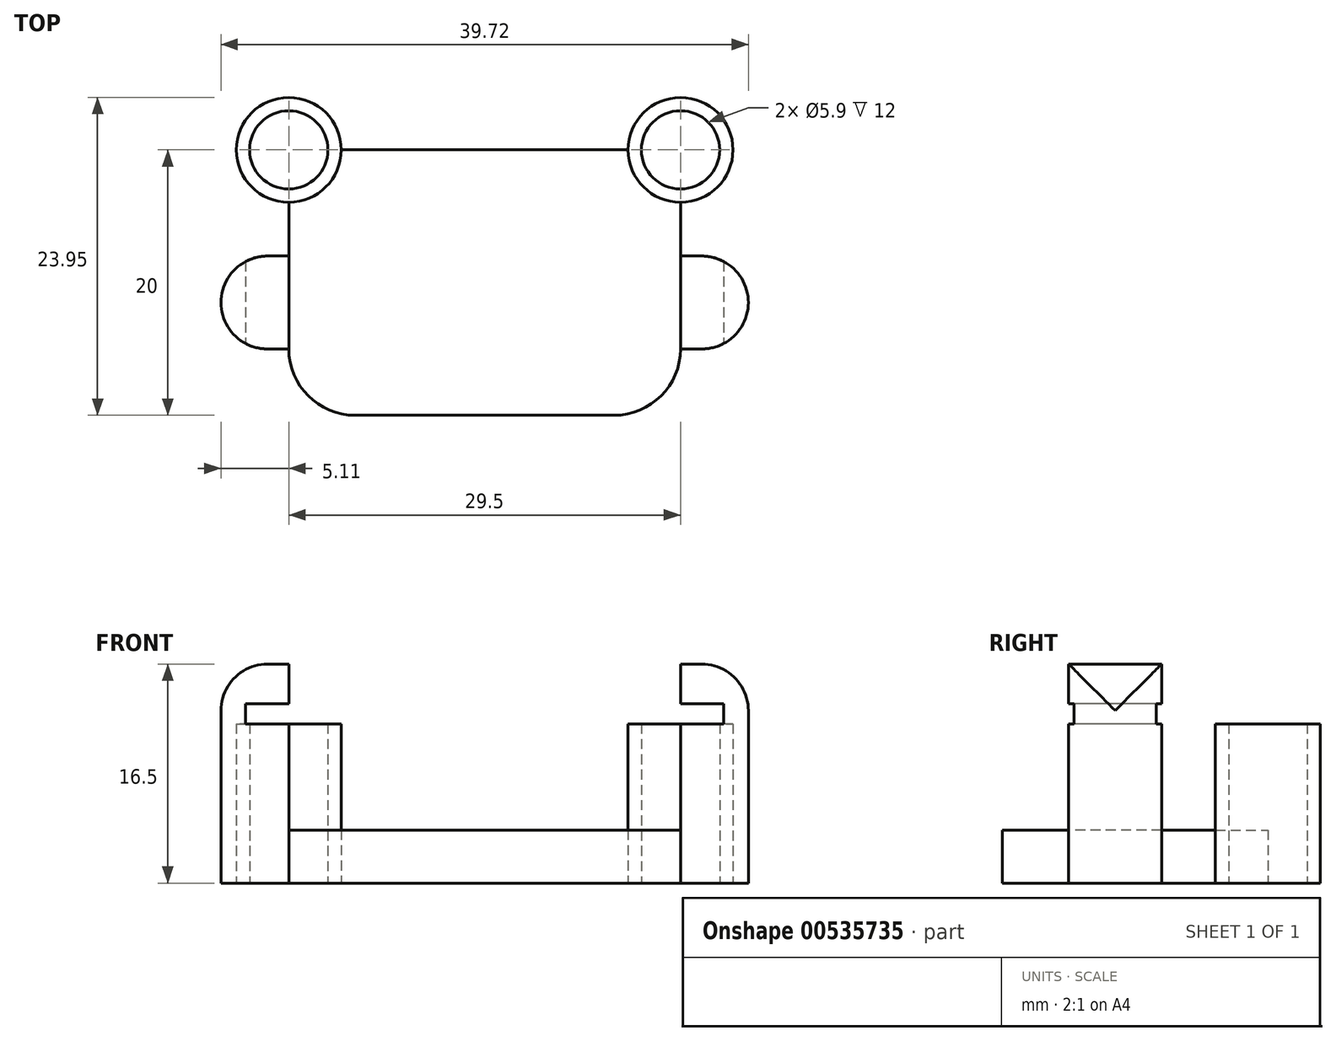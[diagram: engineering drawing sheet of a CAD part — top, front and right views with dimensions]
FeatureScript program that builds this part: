
annotation { "Feature Type Name" : "Feature", "Feature Type Description" : "" }
export const myFeature = defineFeature(function(context is Context, id is Id, definition is map)
    precondition{}
    {
        {
            var Q0;
            Q0=qCreatedBy(makeId("Top.planeOp"),FACE);
            var sketch = newSketch(context, id + "F0", { "sketchPlane" : qUnion([Q0])});
            skCircle(sketch, "E0", {"center": v(0, 0) * mm, "radius": 2.95 * mm});
            skCircle(sketch, "E1", {"center": v(29.5, 0) * mm, "radius": 2.95 * mm});
            skCircle(sketch, "E2", {"center": v(0, 0) * mm, "radius": 3.95 * mm});
            skCircle(sketch, "E3", {"center": v(29.5, 0) * mm, "radius": 3.95 * mm});
            skSolve(sketch);
        }
        {
            var Q0;
            Q0=makeQuery(id+"F0.imprint","IMPRINT",FACE,{"disambiguationData":[TD([[makeQuery(id+"F0.imprint","IMPRINT",EDGE,{"derivedFrom":sQuery(id+"F0.wireOp",EDGE,"E0")}),-1.0]])]});
            var Q1;
            Q1=makeQuery(id+"F0.imprint","IMPRINT",FACE,{"disambiguationData":[TD([[makeQuery(id+"F0.imprint","IMPRINT",EDGE,{"derivedFrom":sQuery(id+"F0.wireOp",EDGE,"E1")}),-1.0]])]});
            extrude(context, id + "F1", {"entities" : qUnion([Q0, Q1]), "depth" : 12 * mm, "offsetDistance" : 25 * mm});
        }
        {
            var Q0;
            Q0=makeQuery(id+"F1.opExtrude","CAP_FACE",FACE,{"disambiguationData":[OSD([sQuery(id+"F0.wireOp",EDGE,"E0"),sQuery(id+"F0.wireOp",EDGE,"E2")])],"isStart":true});
            var sketch = newSketch(context, id + "F2", { "sketchPlane" : qUnion([Q0])});
            skCircle(sketch, "E4.0.0", {"center": v(0, 0) * mm, "radius": 3.95 * mm});
            skCircle(sketch, "E5.0.0", {"center": v(29.5, 0) * mm, "radius": 3.95 * mm});
            skLineSegment(sketch, "E6.bottom", {"start": v(0, 0) * mm, "end": v(29.5, 0) * mm});
            skLineSegment(sketch, "E6.top", {"start": v(0, 20) * mm, "end": v(29.5, 20) * mm});
            skLineSegment(sketch, "E6.left", {"start": v(0, 0) * mm, "end": v(0, 20) * mm});
            skLineSegment(sketch, "E6.right", {"start": v(29.5, 0) * mm, "end": v(29.5, 20) * mm});
            skSolve(sketch);
        }
        {
            var Q0;
            {var subQ0=sQuery(id+"F2.wireOp",EDGE,"E6.top");Q0=makeQuery(id+"F2.imprint","IMPRINT",FACE,{"disambiguationData":[TD([[makeQuery(id+"F2.imprint","IMPRINT",EDGE,{"derivedFrom":subQ0}),-1.0]])]});}
            extrude(context, id + "F3", {"entities" : qUnion([Q0]), "oppositeDirection" : true, "depth" : 4 * mm, "offsetDistance" : 25 * mm});
        }
        {
            var Q0;
            Q0=makeQuery(id+"F3.opExtrude","SWEPT_BODY",BODY,{"disambiguationData":[OSD([sQuery(id+"F2.wireOp",EDGE,"E4.0.0"),sQuery(id+"F2.wireOp",EDGE,"E5.0.0"),sQuery(id+"F2.wireOp",EDGE,"E6.bottom"),sQuery(id+"F2.wireOp",EDGE,"E6.top"),sQuery(id+"F2.wireOp",EDGE,"E6.left"),sQuery(id+"F2.wireOp",EDGE,"E6.right")])]});
            var Q1;
            Q1=makeQuery(id+"F1.opExtrude","SWEPT_BODY",BODY,{"disambiguationData":[OSD([sQuery(id+"F0.wireOp",EDGE,"E0"),sQuery(id+"F0.wireOp",EDGE,"E2")])]});
            var Q2;
            Q2=makeQuery(id+"F1.opExtrude","SWEPT_BODY",BODY,{"disambiguationData":[OSD([sQuery(id+"F0.wireOp",EDGE,"E1"),sQuery(id+"F0.wireOp",EDGE,"E3")])]});
            booleanBodies(context, id + "F4", {"operationType" : BooleanOperationType.UNION, "tools" : qUnion([Q0, Q1, Q2])});
        }
        {
            var Q0;
            Q0=makeQuery(id+"F3.opExtrude","SWEPT_EDGE",EDGE,{"disambiguationData":[OSD([sQuery(id+"F2.wireOp",EDGE,"E6.top"),sQuery(id+"F2.wireOp",EDGE,"E6.left")])]});
            var Q1;
            Q1=makeQuery(id+"F3.opExtrude","SWEPT_EDGE",EDGE,{"disambiguationData":[OSD([sQuery(id+"F2.wireOp",EDGE,"E6.top"),sQuery(id+"F2.wireOp",EDGE,"E6.right")])]});
            fillet(context, id + "F5", {"entities" : qUnion([Q0, Q1]), "radius" : 5 * mm, "tangentPropagation" : true, "allowEdgeOverflow" : false});
        }
        {
            var Q0;
            Q0=makeQuery(id+"F4.opBoolean","MERGE",FACE,{"derivedFrom":[makeQuery(id+"F1.opExtrude","CAP_FACE",FACE,{"disambiguationData":[OSD([sQuery(id+"F0.wireOp",EDGE,"E0"),sQuery(id+"F0.wireOp",EDGE,"E2")])],"isStart":true}),makeQuery(id+"F1.opExtrude","CAP_FACE",FACE,{"disambiguationData":[OSD([sQuery(id+"F0.wireOp",EDGE,"E1"),sQuery(id+"F0.wireOp",EDGE,"E3")])],"isStart":true}),makeQuery(id+"F3.opExtrude","CAP_FACE",FACE,{"disambiguationData":[OSD([sQuery(id+"F2.wireOp",EDGE,"E4.0.0"),sQuery(id+"F2.wireOp",EDGE,"E5.0.0"),sQuery(id+"F2.wireOp",EDGE,"E6.bottom"),sQuery(id+"F2.wireOp",EDGE,"E6.top"),sQuery(id+"F2.wireOp",EDGE,"E6.left"),sQuery(id+"F2.wireOp",EDGE,"E6.right")])],"isStart":true})]});
            var sketch = newSketch(context, id + "F6", { "sketchPlane" : qUnion([Q0])});
            skLineSegment(sketch, "E7.0.0", {"start": v(29.5, 3.95) * mm, "end": v(29.5, 15) * mm});
            skArc(sketch, "E7.0.1", {"start": v(29.5, 15) * mm, "mid": v(28.04, 18.54) * mm, "end": v(24.5, 20) * mm});
            skLineSegment(sketch, "E7.0.2", {"start": v(24.5, 20) * mm, "end": v(5, 20) * mm});
            skArc(sketch, "E7.0.3", {"start": v(5, 20) * mm, "mid": v(1.46, 18.54) * mm, "end": v(0, 15) * mm});
            skLineSegment(sketch, "E7.0.4", {"start": v(0, 15) * mm, "end": v(0, 3.95) * mm});
            skArc(sketch, "E7.0.5", {"start": v(0, 3.95) * mm, "mid": v(-2.8, -2.8) * mm, "end": v(3.95, 0) * mm});
            skLineSegment(sketch, "E7.0.6", {"start": v(3.95, 0) * mm, "end": v(25.55, 0) * mm});
            skArc(sketch, "E7.0.7", {"start": v(25.55, 0) * mm, "mid": v(32.3, -2.8) * mm, "end": v(29.5, 3.95) * mm});
            skLineSegment(sketch, "E8.bottom", {"start": v(0, 15) * mm, "end": v(-2.11, 15) * mm});
            skLineSegment(sketch, "E8.top", {"start": v(0, 8) * mm, "end": v(-2.11, 8) * mm});
            skLineSegment(sketch, "E8.left", {"start": v(0, 15) * mm, "end": v(0, 8) * mm});
            skLineSegment(sketch, "E8.right", {"start": v(-2.11, 15) * mm, "end": v(-2.11, 8) * mm});
            skLineSegment(sketch, "E9.bottom", {"start": v(29.5, 15) * mm, "end": v(31.61, 15) * mm});
            skLineSegment(sketch, "E9.top", {"start": v(29.5, 8) * mm, "end": v(31.61, 8) * mm});
            skLineSegment(sketch, "E9.left", {"start": v(29.5, 15) * mm, "end": v(29.5, 8) * mm});
            skLineSegment(sketch, "E9.right", {"start": v(31.61, 15) * mm, "end": v(31.61, 8) * mm});
            skLineSegment(sketch, "E10.bottom", {"start": v(-2.11, 8) * mm, "end": v(-5.11, 8) * mm});
            skLineSegment(sketch, "E10.top", {"start": v(-2.11, 15) * mm, "end": v(-5.11, 15) * mm});
            skLineSegment(sketch, "E10.left", {"start": v(-2.11, 8) * mm, "end": v(-2.11, 15) * mm});
            skLineSegment(sketch, "E10.right", {"start": v(-5.11, 8) * mm, "end": v(-5.11, 15) * mm});
            skLineSegment(sketch, "E11.bottom", {"start": v(31.61, 8) * mm, "end": v(34.61, 8) * mm});
            skLineSegment(sketch, "E11.top", {"start": v(31.61, 15) * mm, "end": v(34.61, 15) * mm});
            skLineSegment(sketch, "E11.left", {"start": v(31.61, 8) * mm, "end": v(31.61, 15) * mm});
            skLineSegment(sketch, "E11.right", {"start": v(34.61, 8) * mm, "end": v(34.61, 15) * mm});
            skSolve(sketch);
        }
        {
            var Q0;
            Q0=makeQuery(id+"F6.imprint","IMPRINT",FACE,{"disambiguationData":[TD([[makeQuery(id+"F6.imprint","IMPRINT",EDGE,{"derivedFrom":sQuery(id+"F6.wireOp",EDGE,"E10.bottom")}),-1.0]])]});
            var Q1;
            Q1=makeQuery(id+"F6.imprint","IMPRINT",FACE,{"disambiguationData":[TD([[makeQuery(id+"F6.imprint","IMPRINT",EDGE,{"derivedFrom":sQuery(id+"F6.wireOp",EDGE,"E8.bottom")}),1.0]])]});
            var Q2;
            Q2=makeQuery(id+"F6.imprint","IMPRINT",FACE,{"disambiguationData":[TD([[makeQuery(id+"F6.imprint","IMPRINT",EDGE,{"derivedFrom":sQuery(id+"F6.wireOp",EDGE,"E9.bottom")}),-1.0]])]});
            var Q3;
            Q3=makeQuery(id+"F6.imprint","IMPRINT",FACE,{"disambiguationData":[TD([[makeQuery(id+"F6.imprint","IMPRINT",EDGE,{"derivedFrom":sQuery(id+"F6.wireOp",EDGE,"E11.bottom")}),1.0]])]});
            extrude(context, id + "F7", {"entities" : qUnion([Q0, Q1, Q2, Q3]), "operationType" : NewBodyOperationType.ADD, "oppositeDirection" : true, "depth" : 16.5 * mm, "offsetDistance" : 25 * mm});
        }
        {
            var Q0;
            Q0=makeQuery(id+"F7.opExtrude","SWEPT_FACE",FACE,{"disambiguationData":[OSD([sQuery(id+"F6.wireOp",EDGE,"E8.bottom"),sQuery(id+"F6.wireOp",EDGE,"E10.top")])]});
            var sketch = newSketch(context, id + "F8", { "sketchPlane" : qUnion([Q0])});
            skLineSegment(sketch, "E12.0.0", {"start": v(-5.11, 0) * mm, "end": v(0, 0) * mm});
            skLineSegment(sketch, "E12.0.1", {"start": v(0, 0) * mm, "end": v(0, 4) * mm});
            skLineSegment(sketch, "E12.0.2", {"start": v(0, 4) * mm, "end": v(0, 16.5) * mm});
            skLineSegment(sketch, "E12.0.3", {"start": v(0, 16.5) * mm, "end": v(-5.11, 16.5) * mm});
            skLineSegment(sketch, "E12.0.4", {"start": v(-5.11, 16.5) * mm, "end": v(-5.11, 0) * mm});
            skLineSegment(sketch, "E13.0.0", {"start": v(29.5, 0) * mm, "end": v(34.61, 0) * mm});
            skLineSegment(sketch, "E13.0.1", {"start": v(34.61, 0) * mm, "end": v(34.61, 16.5) * mm});
            skLineSegment(sketch, "E13.0.2", {"start": v(34.61, 16.5) * mm, "end": v(29.5, 16.5) * mm});
            skLineSegment(sketch, "E13.0.3", {"start": v(29.5, 16.5) * mm, "end": v(29.5, 4) * mm});
            skLineSegment(sketch, "E13.0.4", {"start": v(29.5, 4) * mm, "end": v(29.5, 0) * mm});
            skLineSegment(sketch, "E14.bottom", {"start": v(0, 13.5) * mm, "end": v(-3.25, 13.5) * mm});
            skLineSegment(sketch, "E14.top", {"start": v(0, 12) * mm, "end": v(-3.25, 12) * mm});
            skLineSegment(sketch, "E14.left", {"start": v(0, 13.5) * mm, "end": v(0, 12) * mm});
            skLineSegment(sketch, "E14.right", {"start": v(-3.25, 13.5) * mm, "end": v(-3.25, 12) * mm});
            skLineSegment(sketch, "E15.bottom", {"start": v(29.5, 13.5) * mm, "end": v(32.75, 13.5) * mm});
            skLineSegment(sketch, "E15.top", {"start": v(29.5, 12) * mm, "end": v(32.75, 12) * mm});
            skLineSegment(sketch, "E15.left", {"start": v(29.5, 13.5) * mm, "end": v(29.5, 12) * mm});
            skLineSegment(sketch, "E15.right", {"start": v(32.75, 13.5) * mm, "end": v(32.75, 12) * mm});
            skSolve(sketch);
        }
        {
            var Q0;
            Q0=makeQuery(id+"F8.imprint","IMPRINT",FACE,{"disambiguationData":[TD([[makeQuery(id+"F8.imprint","IMPRINT",EDGE,{"derivedFrom":sQuery(id+"F8.wireOp",EDGE,"E14.bottom")}),1.0]])]});
            var Q1;
            Q1=makeQuery(id+"F8.imprint","IMPRINT",FACE,{"disambiguationData":[TD([[makeQuery(id+"F8.imprint","IMPRINT",EDGE,{"derivedFrom":sQuery(id+"F8.wireOp",EDGE,"E15.bottom")}),-1.0]])]});
            var Q2;
            Q2=makeQuery(id+"F7.opExtrude","SWEPT_FACE",FACE,{"disambiguationData":[OSD([sQuery(id+"F6.wireOp",EDGE,"E8.top"),sQuery(id+"F6.wireOp",EDGE,"E10.bottom")])]});
            extrude(context, id + "F9", {"entities" : qUnion([Q0, Q1]), "operationType" : NewBodyOperationType.REMOVE, "endBound" : BoundingType.UP_TO_SURFACE, "oppositeDirection" : true, "depth" : 25 * mm, "endBoundEntityFace" : qUnion([Q2]), "offsetDistance" : 25 * mm});
        }
        {
            var Q0;
            Q0=makeQuery(id+"F7.opExtrude","SWEPT_EDGE",EDGE,{"disambiguationData":[OSD([sQuery(id+"F6.wireOp",EDGE,"E10.top"),sQuery(id+"F6.wireOp",EDGE,"E10.right")])]});
            var Q1;
            Q1=makeQuery(id+"F7.opExtrude","SWEPT_EDGE",EDGE,{"disambiguationData":[OSD([sQuery(id+"F6.wireOp",EDGE,"E10.bottom"),sQuery(id+"F6.wireOp",EDGE,"E10.right")])]});
            var Q2;
            Q2=makeQuery(id+"F7.opExtrude","SWEPT_EDGE",EDGE,{"disambiguationData":[OSD([sQuery(id+"F6.wireOp",EDGE,"E11.top"),sQuery(id+"F6.wireOp",EDGE,"E11.right")])]});
            var Q3;
            Q3=makeQuery(id+"F7.opExtrude","SWEPT_EDGE",EDGE,{"disambiguationData":[OSD([sQuery(id+"F6.wireOp",EDGE,"E11.bottom"),sQuery(id+"F6.wireOp",EDGE,"E11.right")])]});
            var Q4;
            Q4=makeQuery(id+"F7.opExtrude","CAP_EDGE",EDGE,{"disambiguationData":[OSD([sQuery(id+"F6.wireOp",EDGE,"E11.right")])],"isStart":false});
            var Q5;
            Q5=makeQuery(id+"F7.opExtrude","CAP_EDGE",EDGE,{"disambiguationData":[OSD([sQuery(id+"F6.wireOp",EDGE,"E10.right")])],"isStart":false});
            fillet(context, id + "F10", {"entities" : qUnion([Q0, Q1, Q2, Q3, Q4, Q5]), "radius" : 3.5 * mm, "tangentPropagation" : true, "allowEdgeOverflow" : false});
        }
    });
